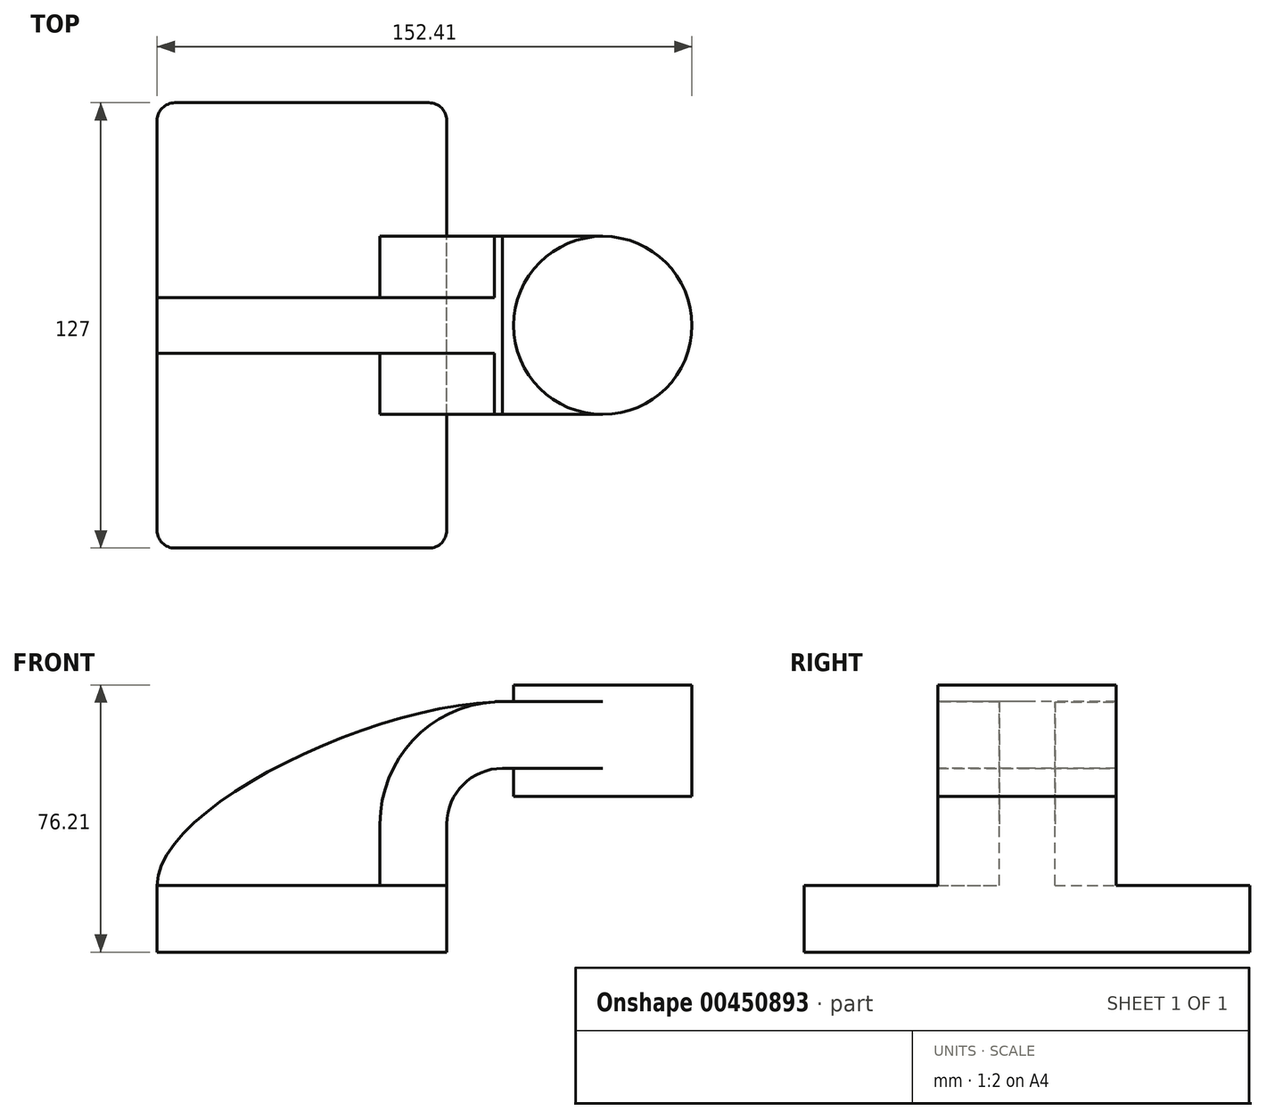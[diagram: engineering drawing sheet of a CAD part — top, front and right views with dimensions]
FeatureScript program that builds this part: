
annotation { "Feature Type Name" : "Feature", "Feature Type Description" : "" }
export const myFeature = defineFeature(function(context is Context, id is Id, definition is map)
    precondition{}
    {
        {
            var Q0;
            Q0=qCreatedBy(makeId("Front.planeOp"),FACE);
            var sketch = newSketch(context, id + "F0", { "sketchPlane" : qUnion([Q0])});
            skLineSegment(sketch, "E0.bottom", {"start": v(41.27, 9.53) * mm, "end": v(-41.28, 9.53) * mm});
            skLineSegment(sketch, "E0.top", {"start": v(41.28, -9.52) * mm, "end": v(-41.27, -9.52) * mm});
            skLineSegment(sketch, "E0.left", {"start": v(41.28, 9.53) * mm, "end": v(41.28, -9.52) * mm});
            skLineSegment(sketch, "E0.right", {"start": v(-41.28, 9.53) * mm, "end": v(-41.27, -9.52) * mm});
            skPoint(sketch, "E0.middle", {"position": v(0, 0) * mm});
            skLineSegment(sketch, "E1", {"start": v(41.27, 9.53) * mm, "end": v(41.27, 27) * mm});
            skArc(sketch, "E2", {"start": v(41.27, 27) * mm, "mid": v(45.92, 38.23) * mm, "end": v(57.15, 42.88) * mm});
            skLineSegment(sketch, "E3", {"start": v(57.15, 42.88) * mm, "end": v(85.73, 42.88) * mm});
            skLineSegment(sketch, "E4.bottom", {"start": v(111.13, 66.68) * mm, "end": v(60.33, 66.68) * mm});
            skLineSegment(sketch, "E4.top", {"start": v(111.13, 34.93) * mm, "end": v(60.33, 34.92) * mm});
            skLineSegment(sketch, "E4.left", {"start": v(111.13, 66.68) * mm, "end": v(111.13, 34.93) * mm});
            skLineSegment(sketch, "E4.right", {"start": v(60.33, 66.68) * mm, "end": v(60.33, 34.93) * mm});
            skPoint(sketch, "E4.middle", {"position": v(85.73, 50.8) * mm});
            skLineSegment(sketch, "E5.0", {"start": v(57.15, 61.93) * mm, "end": v(85.73, 61.93) * mm});
            skArc(sketch, "E5.1", {"start": v(22.23, 27) * mm, "mid": v(32.45, 51.7) * mm, "end": v(57.15, 61.93) * mm});
            skLineSegment(sketch, "E5.2", {"start": v(22.22, 9.53) * mm, "end": v(22.22, 27) * mm});
            skFitSpline(sketch, "E6", {"points": [v(-41.28, 9.53) * mm, v(57.15, 61.93) * mm], "startDerivative": vector(-0.1, 66.38) * mm, "endDerivative": vector(111.62, 2.02) * mm});
            skLineSegment(sketch, "E7", {"start": v(85.73, 34.92) * mm, "end": v(85.73, 66.68) * mm});
            skSolve(sketch);
        }
        {
            var Q0;
            Q0=makeQuery(id+"F0.imprint","IMPRINT",FACE,{"disambiguationData":[TD([[makeQuery(id+"F0.imprint","IMPRINT",EDGE,{"derivedFrom":sQuery(id+"F0.wireOp",EDGE,"E0.top")}),-1.0]])]});
            extrude(context, id + "F1", {"entities" : qUnion([Q0]), "endBound" : BoundingType.SYMMETRIC, "depth" : 127 * mm});
        }
        {
            var Q0;
            {var subQ9=sQuery(id+"F0.wireOp",EDGE,"E1");Q0=makeQuery(id+"F0.imprint","IMPRINT",FACE,{"disambiguationData":[TD([[makeQuery(id+"F0.imprint","IMPRINT",EDGE,{"derivedFrom":subQ9}),1.0]])]});}
            var Q1;
            {var subQ0=sQuery(id+"F0.wireOp",EDGE,"E7");var subQ1=sQuery(id+"F0.wireOp",EDGE,"E3");var subQ2=makeQuery(id+"F0.imprint","INTERSECT",VERTEX,{"derivedFrom":[subQ1,subQ0]});Q1=makeQuery(id+"F0.imprint","IMPRINT",FACE,{"disambiguationData":[TD([[makeQuery(id+"F0.imprint","IMPRINT",EDGE,{"disambiguationData":[TD([[subQ2,1.0]])],"derivedFrom":subQ1}),1.0]])]});}
            extrude(context, id + "F2", {"entities" : qUnion([Q0, Q1]), "operationType" : NewBodyOperationType.ADD, "endBound" : BoundingType.SYMMETRIC, "depth" : 50.8 * mm});
        }
        {
            var Q0;
            {var subQ3=sQuery(id+"F0.wireOp",EDGE,"E5.2");Q0=makeQuery(id+"F0.imprint","IMPRINT",FACE,{"disambiguationData":[TD([[makeQuery(id+"F0.imprint","IMPRINT",EDGE,{"derivedFrom":subQ3}),1.0]])]});}
            extrude(context, id + "F3", {"entities" : qUnion([Q0]), "operationType" : NewBodyOperationType.ADD, "endBound" : BoundingType.SYMMETRIC, "depth" : 15.88 * mm});
        }
        {
            var Q0;
            {var subQ0=sQuery(id+"F0.wireOp",EDGE,"E4.left");Q0=makeQuery(id+"F0.imprint","IMPRINT",FACE,{"disambiguationData":[TD([[makeQuery(id+"F0.imprint","IMPRINT",EDGE,{"derivedFrom":subQ0}),-1.0]])]});}
            var Q1;
            Q1=sQuery(id+"F0.wireOp",EDGE,"E7");
            revolve(context, id + "F4", {"operationType" : NewBodyOperationType.ADD, "entities" : qUnion([Q0]), "axis" : qUnion([Q1]), "revolveType" : RevolveType.FULL});
        }
        {
            var Q0;
            Q0=makeQuery(id+"F1.opExtrude","CAP_EDGE",EDGE,{"disambiguationData":[OSD([sQuery(id+"F0.wireOp",EDGE,"E0.right")])],"isStart":false});
            var Q1;
            Q1=makeQuery(id+"F1.opExtrude","CAP_EDGE",EDGE,{"disambiguationData":[OSD([sQuery(id+"F0.wireOp",EDGE,"E0.left")])],"isStart":false});
            var Q2;
            Q2=makeQuery(id+"F1.opExtrude","CAP_EDGE",EDGE,{"disambiguationData":[OSD([sQuery(id+"F0.wireOp",EDGE,"E0.left")])],"isStart":true});
            var Q3;
            Q3=makeQuery(id+"F1.opExtrude","CAP_EDGE",EDGE,{"disambiguationData":[OSD([sQuery(id+"F0.wireOp",EDGE,"E0.right")])],"isStart":true});
            fillet(context, id + "F5", {"entities" : qUnion([Q0, Q1, Q2, Q3]), "radius" : 5.08 * mm, "tangentPropagation" : true, "allowEdgeOverflow" : false});
        }
    });
